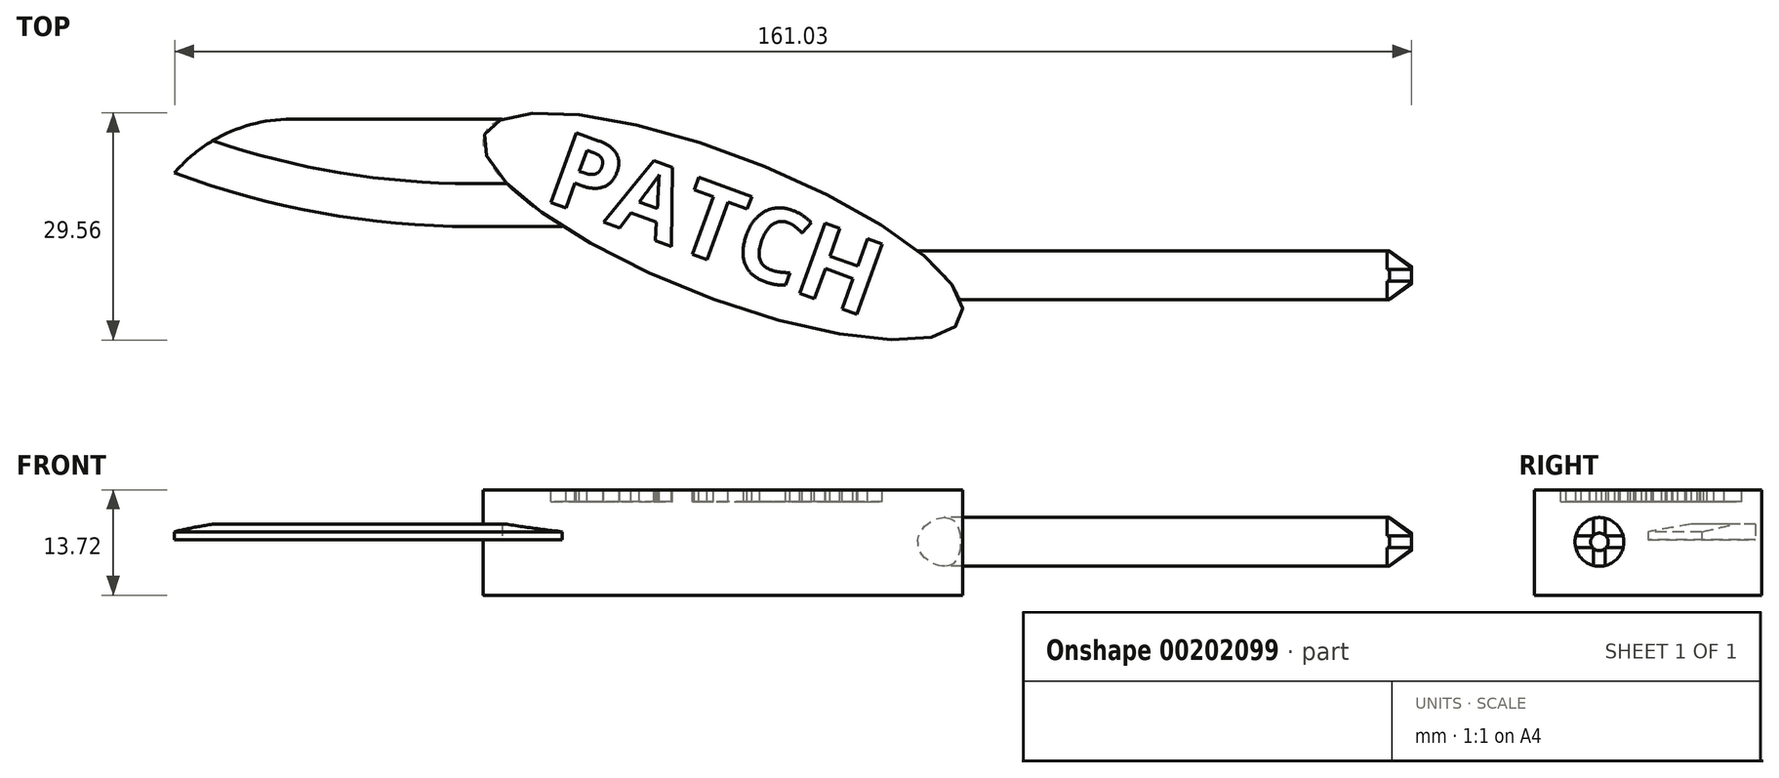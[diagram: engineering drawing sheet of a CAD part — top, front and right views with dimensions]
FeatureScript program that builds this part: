
annotation { "Feature Type Name" : "Feature", "Feature Type Description" : "" }
export const myFeature = defineFeature(function(context is Context, id is Id, definition is map)
    precondition{}
    {
        {
            var Q0;
            Q0=qCreatedBy(makeId("Top.planeOp"),FACE);
            var sketch = newSketch(context, id + "F0", { "sketchPlane" : qUnion([Q0])});
            skEllipse(sketch, "E0", {"center": v(0, 0) * mm, "majorRadius": 33.25 * mm, "minorRadius": 9.29 * mm, "majorAxis": v(-0.93, 0.36)});
            skLineSegment(sketch, "E1", {"start": v(-3.76, 11.15) * mm, "end": v(-7.76, 28.1) * mm});
            skLineSegment(sketch, "E2", {"start": v(-7.76, 28.1) * mm, "end": v(0, 9.9) * mm});
            skSolve(sketch);
        }
        {
            var Q0;
            {var subQ0=sQuery(id+"F0.wireOp",EDGE,"E0");var subQ1=makeQuery(id+"F0.imprint","INTERSECT",VERTEX,{"derivedFrom":[subQ0,sQuery(id+"F0.wireOp",EDGE,"E1")]});Q0=makeQuery(id+"F0.imprint","IMPRINT",FACE,{"disambiguationData":[TD([[makeQuery(id+"F0.imprint","IMPRINT",EDGE,{"disambiguationData":[TD([[subQ1,1.0]])],"derivedFrom":subQ0}),1.0]])]});}
            extrude(context, id + "F1", {"entities" : qUnion([Q0]), "depth" : 13.72 * mm});
        }
        {
            var Q0;
            Q0=qCreatedBy(makeId("Right.planeOp"),FACE);
            var sketch = newSketch(context, id + "F2", { "sketchPlane" : qUnion([Q0])});
            skCircle(sketch, "E3", {"center": v(-6.35, 6.95) * mm, "radius": 3.18 * mm});
            skSolve(sketch);
        }
        {
            var Q0;
            Q0 = qSketchRegion(id + "F2", true);
            var Q1;
            Q1=sQuery(id+"F2.wireOp",EDGE,"E3");
            extrude(context, id + "F3", {"entities" : qUnion([Q0]), "operationType" : NewBodyOperationType.ADD, "surfaceEntities" : qUnion([Q1]), "depth" : 64.26 * mm});
        }
        {
            var Q0;
            Q0=makeQuery(id+"F3.opExtrude","CAP_FACE",FACE,{"disambiguationData":[OSD([sQuery(id+"F2.wireOp",EDGE,"E3")])],"isStart":false});
            extrude(context, id + "F4", {"entities" : qUnion([Q0]), "operationType" : NewBodyOperationType.ADD, "depth" : 25.4 * mm});
        }
        {
            var Q0;
            Q0=makeQuery(id+"F4.opExtrude","CAP_FACE",FACE,{"disambiguationData":[OSD([sQuery(id+"F2.wireOp",EDGE,"E3")])],"isStart":false});
            var sketch = newSketch(context, id + "F5", { "sketchPlane" : qUnion([Q0])});
            skLineSegment(sketch, "E4", {"start": v(-5.59, 11.79) * mm, "end": v(-5.59, 7.7) * mm});
            skLineSegment(sketch, "E5", {"start": v(-5.59, 7.7) * mm, "end": v(-1.1, 7.7) * mm});
            skLineSegment(sketch, "E6", {"start": v(-1.1, 7.7) * mm, "end": v(-1.1, 6.18) * mm});
            skLineSegment(sketch, "E7", {"start": v(-1.1, 6.18) * mm, "end": v(-5.59, 6.18) * mm});
            skLineSegment(sketch, "E8", {"start": v(-5.59, 6.18) * mm, "end": v(-5.59, 1.9) * mm});
            skLineSegment(sketch, "E9", {"start": v(-5.59, 1.9) * mm, "end": v(-7.11, 1.9) * mm});
            skLineSegment(sketch, "E10", {"start": v(-7.11, 1.9) * mm, "end": v(-7.11, 6.18) * mm});
            skLineSegment(sketch, "E11", {"start": v(-7.11, 6.18) * mm, "end": v(-11.64, 6.18) * mm});
            skLineSegment(sketch, "E12", {"start": v(-11.64, 6.18) * mm, "end": v(-11.64, 7.7) * mm});
            skLineSegment(sketch, "E13", {"start": v(-11.64, 7.7) * mm, "end": v(-7.11, 7.7) * mm});
            skLineSegment(sketch, "E14", {"start": v(-7.11, 7.7) * mm, "end": v(-7.11, 11.79) * mm});
            skLineSegment(sketch, "E15", {"start": v(-7.11, 11.79) * mm, "end": v(-5.59, 11.79) * mm});
            skLineSegment(sketch, "E16", {"start": v(-6.35, 14.64) * mm, "end": v(-6.35, 0.68) * mm, "construction": true});
            skPoint(sketch, "E16.endSnap0", {"position": v(-6.35, 1.9) * mm});
            skLineSegment(sketch, "E17", {"start": v(-14.38, 6.95) * mm, "end": v(2, 6.95) * mm, "construction": true});
            skCircle(sketch, "E18", {"center": v(-6.35, 6.95) * mm, "radius": 0.94 * mm, "construction": true});
            skSolve(sketch);
        }
        {
            var Q0;
            {var subQ0=sQuery(id+"F5.wireOp",EDGE,"E5");var subQ1=sQuery(id+"F5.wireOp",EDGE,"E4");var subQ2=makeQuery(id+"F5.imprint","INTERSECT",VERTEX,{"derivedFrom":[subQ1,subQ0]});Q0=makeQuery(id+"F5.imprint","IMPRINT",FACE,{"disambiguationData":[TD([[makeQuery(id+"F5.imprint","IMPRINT",EDGE,{"disambiguationData":[TD([[subQ2,1.0]])],"derivedFrom":subQ1}),1.0]])]});}
            var Q1;
            {var subQ0=sQuery(id+"F5.wireOp",EDGE,"E14");var subQ1=sQuery(id+"F5.wireOp",EDGE,"E13");var subQ2=makeQuery(id+"F5.imprint","INTERSECT",VERTEX,{"derivedFrom":[subQ1,subQ0]});Q1=makeQuery(id+"F5.imprint","IMPRINT",FACE,{"disambiguationData":[TD([[makeQuery(id+"F5.imprint","IMPRINT",EDGE,{"disambiguationData":[TD([[subQ2,1.0]])],"derivedFrom":subQ1}),1.0]])]});}
            var Q2;
            {var subQ0=sQuery(id+"F5.wireOp",EDGE,"E11");var subQ1=sQuery(id+"F5.wireOp",EDGE,"E10");var subQ2=makeQuery(id+"F5.imprint","INTERSECT",VERTEX,{"derivedFrom":[subQ1,subQ0]});Q2=makeQuery(id+"F5.imprint","IMPRINT",FACE,{"disambiguationData":[TD([[makeQuery(id+"F5.imprint","IMPRINT",EDGE,{"disambiguationData":[TD([[subQ2,1.0]])],"derivedFrom":subQ1}),1.0]])]});}
            var Q3;
            {var subQ0=sQuery(id+"F5.wireOp",EDGE,"E8");var subQ1=sQuery(id+"F5.wireOp",EDGE,"E7");var subQ2=makeQuery(id+"F5.imprint","INTERSECT",VERTEX,{"derivedFrom":[subQ1,subQ0]});Q3=makeQuery(id+"F5.imprint","IMPRINT",FACE,{"disambiguationData":[TD([[makeQuery(id+"F5.imprint","IMPRINT",EDGE,{"disambiguationData":[TD([[subQ2,1.0]])],"derivedFrom":subQ1}),1.0]])]});}
            extrude(context, id + "F6", {"entities" : qUnion([Q0, Q1, Q2, Q3]), "operationType" : NewBodyOperationType.REMOVE, "oppositeDirection" : true, "depth" : 3.17 * mm});
        }
        {
            var Q0;
            {var subQ0=sQuery(id+"F2.wireOp",EDGE,"E3");Q0=makeQuery(id+"F6.boolean.opBoolean","SPLIT",EDGE,{"disambiguationData":[TD([makeQuery(id+"F6.opExtrude","SWEPT_FACE",FACE,{"disambiguationData":[OSD([sQuery(id+"F5.wireOp",EDGE,"E11")])]})])],"derivedFrom":makeQuery(id+"F4.opExtrude","CAP_EDGE",EDGE,{"disambiguationData":[OSD([subQ0])],"isStart":false})});}
            var Q1;
            {var subQ0=sQuery(id+"F2.wireOp",EDGE,"E3");Q1=makeQuery(id+"F6.boolean.opBoolean","SPLIT",EDGE,{"disambiguationData":[TD([makeQuery(id+"F6.opExtrude","SWEPT_FACE",FACE,{"disambiguationData":[OSD([sQuery(id+"F5.wireOp",EDGE,"E8")])]})])],"derivedFrom":makeQuery(id+"F4.opExtrude","CAP_EDGE",EDGE,{"disambiguationData":[OSD([subQ0])],"isStart":false})});}
            var Q2;
            {var subQ0=sQuery(id+"F2.wireOp",EDGE,"E3");Q2=makeQuery(id+"F6.boolean.opBoolean","SPLIT",EDGE,{"disambiguationData":[TD([makeQuery(id+"F6.opExtrude","SWEPT_FACE",FACE,{"disambiguationData":[OSD([sQuery(id+"F5.wireOp",EDGE,"E5")])]})])],"derivedFrom":makeQuery(id+"F4.opExtrude","CAP_EDGE",EDGE,{"disambiguationData":[OSD([subQ0])],"isStart":false})});}
            var Q3;
            {var subQ0=sQuery(id+"F2.wireOp",EDGE,"E3");Q3=makeQuery(id+"F6.boolean.opBoolean","SPLIT",EDGE,{"disambiguationData":[TD([makeQuery(id+"F6.opExtrude","SWEPT_FACE",FACE,{"disambiguationData":[OSD([sQuery(id+"F5.wireOp",EDGE,"E4")])]})])],"derivedFrom":makeQuery(id+"F4.opExtrude","CAP_EDGE",EDGE,{"disambiguationData":[OSD([subQ0])],"isStart":false})});}
            chamfer(context, id + "F7", {"entities" : qUnion([Q0, Q1, Q2, Q3]), "chamferType" : ChamferType.OFFSET_ANGLE, "width" : 2.03 * mm, "oppositeDirection" : false, "angle" : 55 * degree});
        }
        {
            var Q0;
            Q0=qCreatedBy(makeId("Right.planeOp"),FACE);
            var sketch = newSketch(context, id + "F8", { "sketchPlane" : qUnion([Q0])});
            skLineSegment(sketch, "E19.bottom", {"start": v(13.97, 7.22) * mm, "end": v(0, 7.22) * mm});
            skLineSegment(sketch, "E19.top", {"start": v(13.97, 9.25) * mm, "end": v(0, 9.25) * mm});
            skLineSegment(sketch, "E19.left", {"start": v(13.97, 7.22) * mm, "end": v(13.97, 9.25) * mm});
            skLineSegment(sketch, "E19.right", {"start": v(0, 7.22) * mm, "end": v(0, 9.25) * mm});
            skSolve(sketch);
        }
        {
            var Q0;
            Q0 = qSketchRegion(id + "F8", true);
            extrude(context, id + "F9", {"entities" : qUnion([Q0]), "operationType" : NewBodyOperationType.ADD, "oppositeDirection" : true, "depth" : 71.37 * mm});
        }
        {
            var Q0;
            {var subQ0=sQuery(id+"F8.wireOp",EDGE,"E19.right");var subQ2=sQuery(id+"F8.wireOp",EDGE,"E19.bottom");Q0=makeQuery(id+"F9.boolean.opBoolean","SPLIT",FACE,{"disambiguationData":[TD([makeQuery(id+"F9.opExtrude","SWEPT_FACE",FACE,{"disambiguationData":[OSD([subQ0])]})])],"derivedFrom":makeQuery(id+"F9.opExtrude","SWEPT_FACE",FACE,{"disambiguationData":[OSD([subQ2])]})});}
            var sketch = newSketch(context, id + "F10", { "sketchPlane" : qUnion([Q0])});
            skArc(sketch, "E20", {"start": v(-71.37, -6.99) * mm, "mid": v(-64.54, -12.14) * mm, "end": v(-56.18, -13.97) * mm});
            skArc(sketch, "E21", {"start": v(-32.7, 0) * mm, "mid": v(-52.35, -1.76) * mm, "end": v(-71.37, -6.99) * mm});
            skPoint(sketch, "E22", {"position": v(-50.05, -13.97) * mm});
            skSolve(sketch);
        }
        {
            var Q0;
            {var subQ0=sQuery(id+"F10.wireOp",EDGE,"E20");Q0=makeQuery(id+"F10.imprint","IMPRINT",FACE,{"disambiguationData":[TD([[makeQuery(id+"F10.imprint","IMPRINT",EDGE,{"derivedFrom":subQ0}),-1.0]])]});}
            var Q1;
            {var subQ0=sQuery(id+"F10.wireOp",EDGE,"E21");Q1=makeQuery(id+"F10.imprint","IMPRINT",FACE,{"disambiguationData":[TD([[makeQuery(id+"F10.imprint","IMPRINT",EDGE,{"derivedFrom":subQ0}),-1.0]])]});}
            extrude(context, id + "F11", {"entities" : qUnion([Q0, Q1]), "operationType" : NewBodyOperationType.REMOVE, "oppositeDirection" : true, "depth" : 10.67 * mm});
        }
        {
            var Q0;
            Q0=makeQuery(id+"F11.boolean.opBoolean","COPY",EDGE,{"derivedFrom":makeQuery(id+"F11.opExtrude","CAP_EDGE",EDGE,{"disambiguationData":[OSD([sQuery(id+"F10.wireOp",EDGE,"E21")])],"isStart":true})});
            var Q1;
            {var subQ0=sQuery(id+"F8.wireOp",EDGE,"E19.right");var subQ2=sQuery(id+"F8.wireOp",EDGE,"E19.top");Q1=makeQuery(id+"F11.boolean.opBoolean","INTERSECT",EDGE,{"derivedFrom":[makeQuery(id+"F9.boolean.opBoolean","SPLIT",FACE,{"disambiguationData":[TD([makeQuery(id+"F9.opExtrude","SWEPT_FACE",FACE,{"disambiguationData":[OSD([subQ0])]})])],"derivedFrom":makeQuery(id+"F9.opExtrude","SWEPT_FACE",FACE,{"disambiguationData":[OSD([subQ2])]})}),makeQuery(id+"F11.opExtrude","SWEPT_FACE",FACE,{"disambiguationData":[OSD([sQuery(id+"F10.wireOp",EDGE,"E21")])]})]});}
            chamfer(context, id + "F12", {"entities" : qUnion([Q0, Q1]), "chamferType" : ChamferType.OFFSET_ANGLE, "width" : 5.6 * mm, "oppositeDirection" : false, "angle" : 10 * degree, "tangentPropagation" : true});
        }
        {
            var Q0;
            Q0=makeQuery(id+"F1.opExtrude","CAP_FACE",FACE,{"disambiguationData":[OSD([sQuery(id+"F0.wireOp",EDGE,"E0")])],"isStart":false});
            var sketch = newSketch(context, id + "F13", { "sketchPlane" : qUnion([Q0])});
            skText(sketch, "E23", { "text": "PATCH", "fontName": "OpenSans-Bold.ttf"});
            skLineSegment(sketch, "E24", {"start": v(-46.92, 22.41) * mm, "end": v(54.33, -14.44) * mm, "construction": true});
            const initialGuessF13  = {"E23": [-0.02352, 0.0035, 0.9397, -0.34202, 0.00978]};
            skSetInitialGuess(sketch, initialGuessF13);
            skSolve(sketch);
        }
        {
            var Q0;
            Q0 = qSketchRegion(id + "F13", true);
            extrude(context, id + "F14", {"entities" : qUnion([Q0]), "operationType" : NewBodyOperationType.REMOVE, "oppositeDirection" : true, "depth" : 1.52 * mm});
        }
        {
            var Q0;
            {var subQ0=sQuery(id+"F8.wireOp",EDGE,"E19.left");var subQ1=sQuery(id+"F8.wireOp",EDGE,"E19.top");Q0=makeQuery(id+"F9.boolean.opBoolean","SPLIT",FACE,{"disambiguationData":[TD([makeQuery(id+"F9.opExtrude","CAP_FACE",FACE,{"disambiguationData":[OSD([sQuery(id+"F8.wireOp",EDGE,"E19.bottom"),subQ1,subQ0,sQuery(id+"F8.wireOp",EDGE,"E19.right")])],"isStart":true})])],"derivedFrom":makeQuery(id+"F9.opExtrude","SWEPT_FACE",FACE,{"disambiguationData":[OSD([subQ1])]})});}
            extrude(context, id + "F15", {"entities" : qUnion([Q0]), "operationType" : NewBodyOperationType.REMOVE, "oppositeDirection" : true, "depth" : 25.4 * mm});
        }
    });
